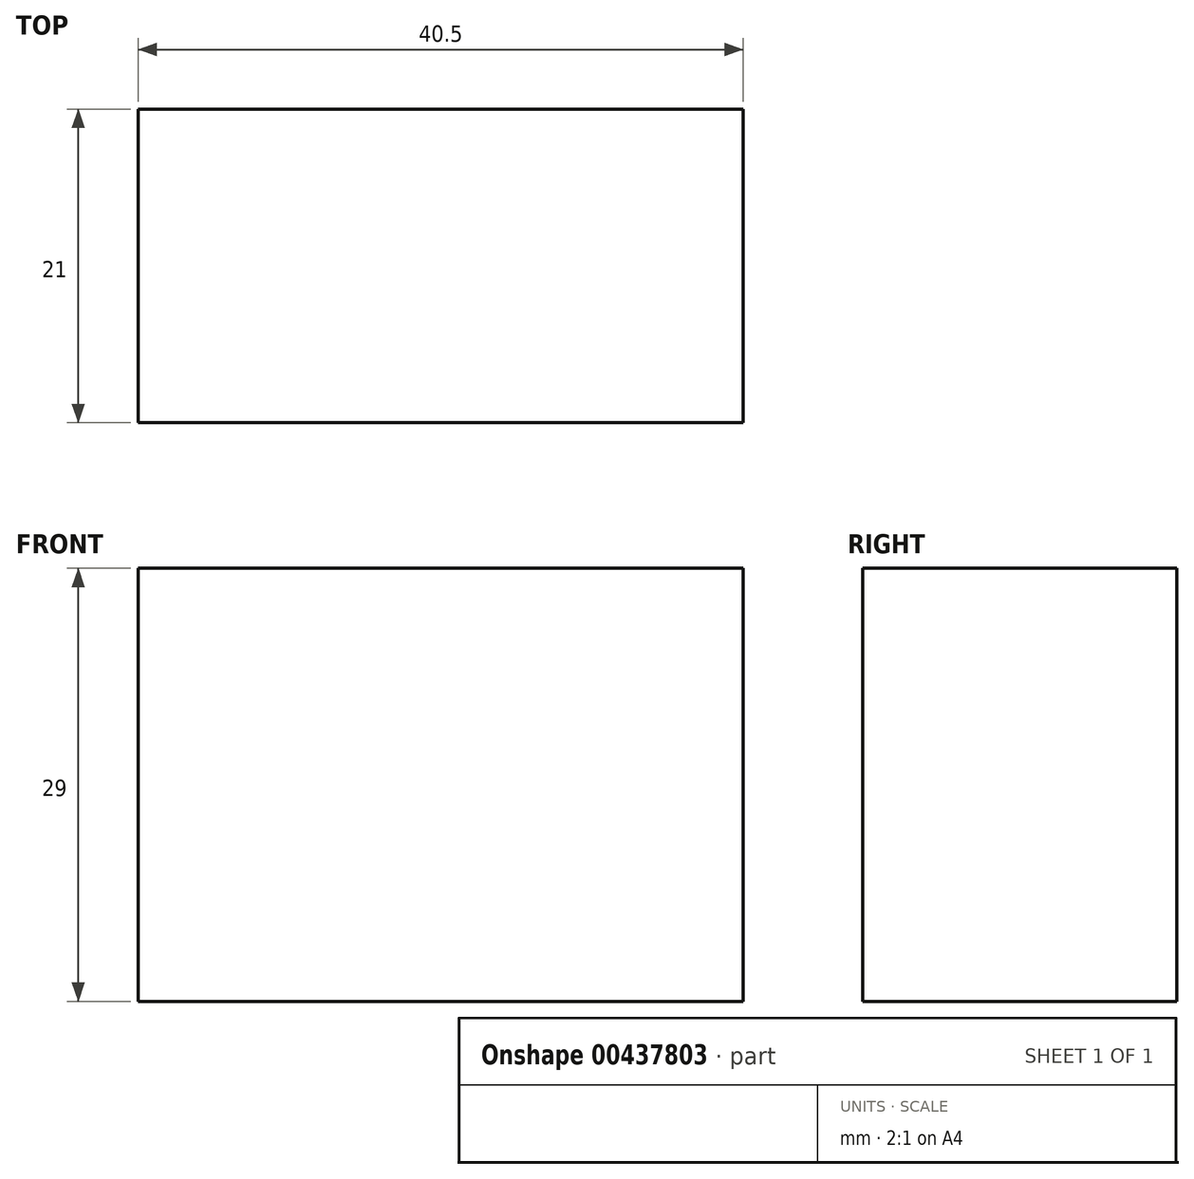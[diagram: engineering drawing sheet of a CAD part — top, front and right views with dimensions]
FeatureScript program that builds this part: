
annotation { "Feature Type Name" : "Feature", "Feature Type Description" : "" }
export const myFeature = defineFeature(function(context is Context, id is Id, definition is map)
    precondition{}
    {
        {
            var Q0;
            Q0=qCreatedBy(makeId("Top.planeOp"),FACE);
            var sketch = newSketch(context, id + "F0", { "sketchPlane" : qUnion([Q0])});
            skLineSegment(sketch, "E0.bottom", {"start": v(20.25, 10.5) * mm, "end": v(-20.25, 10.5) * mm});
            skLineSegment(sketch, "E0.top", {"start": v(20.25, -10.5) * mm, "end": v(-20.25, -10.5) * mm});
            skLineSegment(sketch, "E0.left", {"start": v(20.25, 10.5) * mm, "end": v(20.25, -10.5) * mm});
            skLineSegment(sketch, "E0.right", {"start": v(-20.25, 10.5) * mm, "end": v(-20.25, -10.5) * mm});
            skPoint(sketch, "E0.middle", {"position": v(0, 0) * mm});
            skSolve(sketch);
        }
        {
            var Q0;
            Q0=makeQuery(id+"F0.imprint","IMPRINT",FACE,{"disambiguationData":[TD([[makeQuery(id+"F0.imprint","IMPRINT",EDGE,{"derivedFrom":sQuery(id+"F0.wireOp",EDGE,"E0.bottom")}),1.0]])]});
            extrude(context, id + "F1", {"entities" : qUnion([Q0]), "oppositeDirection" : true, "depth" : 29 * mm});
        }
    });
